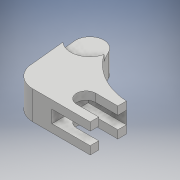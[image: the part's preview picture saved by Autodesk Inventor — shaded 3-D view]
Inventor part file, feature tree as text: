
AUTODESK INVENTOR PART (.ipt)
format: ipt  version: 2018 (Build 220112000, 112)  size: 152,064 bytes
history: native  units: mm
features: extrude x4, sketch x4
ambient origin geometry x8: Origin, YZ Plane, XZ Plane, XY Plane, X Axis, Y Axis, Z Axis, Center Point
bodies: Solid1 (feature_tree)
feature tree (8):
  extrude  "Extrusion1"  Depth=28.0mm
  extrude  "Extrusion2"  Depth=36.0mm
  extrude  "Extrusion3"  Depth=28.52mm TaperAngle=0.0deg
  extrude  "Extrusion4"  Depth=6.0mm TaperAngle=0.0deg
  sketch  "Sketch1"  dims[d0=44.0mm d3=28.0mm]
  sketch  "Sketch2"  dims[d4=57.0mm d5=36.0mm]
  sketch  "Sketch4"  dims[d6=67.0mm d7=28.52mm d8=0.0mm]
  sketch  "Sketch5"  dims[d9=38.0mm d10=6.0mm d11=0.0mm d17=19.05mm d19=22.0mm d20=28.52mm d21=0.0mm d22=8.0mm d23=8.0mm d24=8.0mm d25=0.0mm d26=8.0mm d27=12.52mm d28=38.0mm d29=0.0mm]
